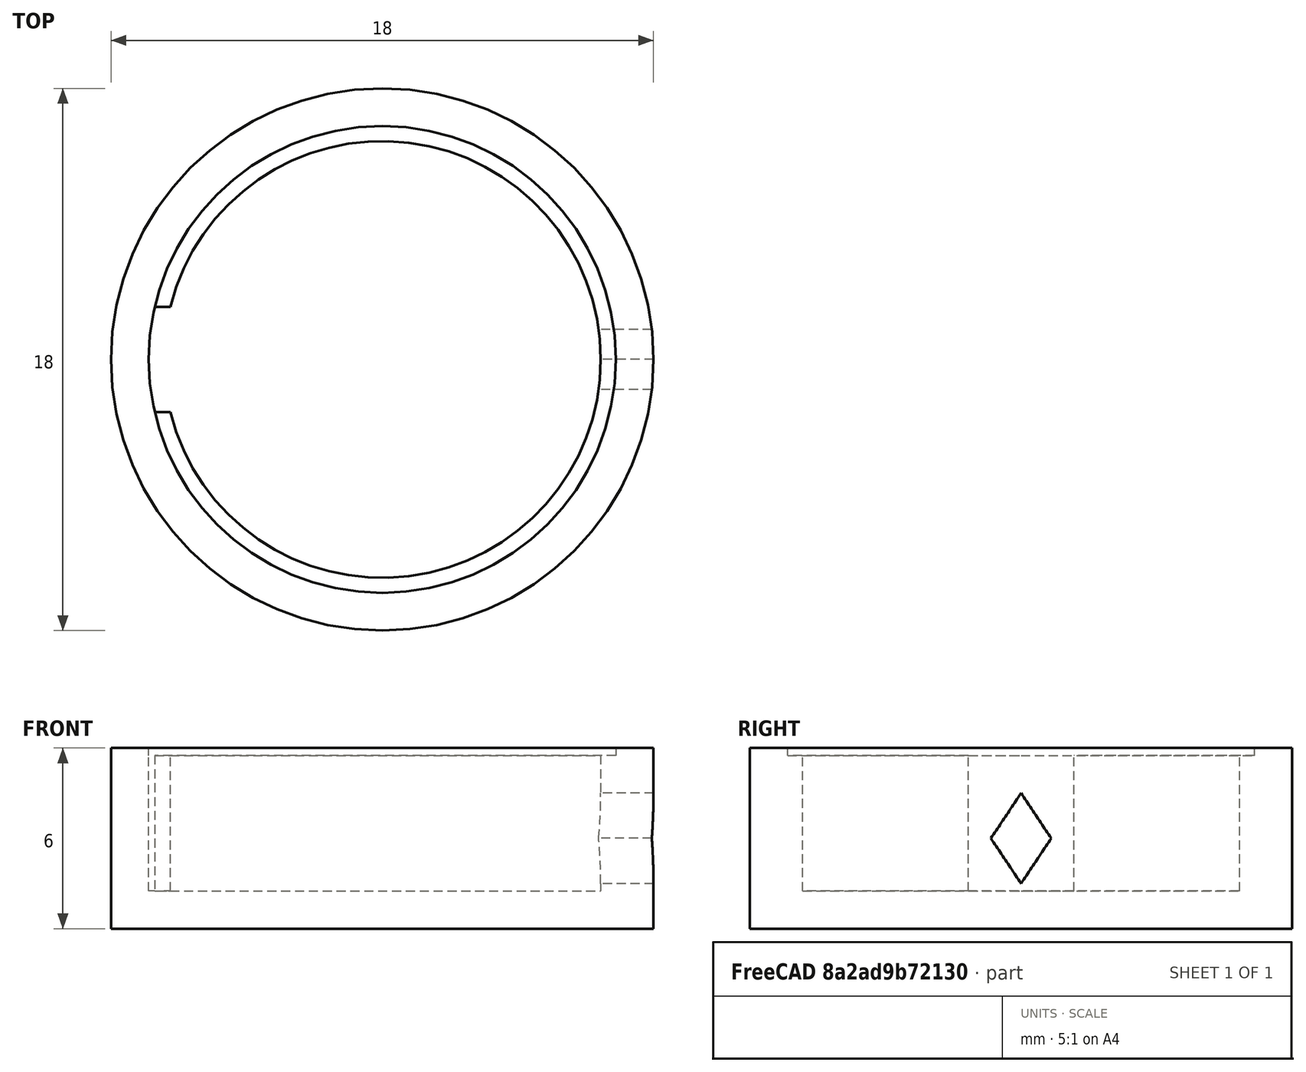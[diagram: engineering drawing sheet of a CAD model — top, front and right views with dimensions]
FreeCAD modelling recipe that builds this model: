
FCSTD DOCUMENT  (FreeCAD 0.17R13541 (Git))
Label: PiezoBlob
License: All rights reserved
LicenseURL: http://en.wikipedia.org/wiki/All_rights_reserved
objects: Sketcher::SketchObject×5, PartDesign::Pocket×4, PartDesign::Pad×1, PartDesign::Plane×1, PartDesign::Body×1, Mesh::Feature×1
note: 17 computed .brp shape members not serialized (recipe doc carries the construction recipe); baked Part::Feature solids carry a one-line shape summary decoded from their .brp

FEATURE [Sketcher::SketchObject] Sketch
  MapMode = 5
  Support = -> [XY_Plane]
  sketch-geometry (2):
    g0: Circle [constr] CenterX=0 CenterY=0 CenterZ=0 NormalX=0 NormalY=0 NormalZ=1 AngleXU=0 Radius=7.5
    g1: Circle CenterX=0 CenterY=0 CenterZ=0 NormalX=0 NormalY=0 NormalZ=1 AngleXU=0 Radius=9
  constraints (4):
    c: Coincident(g0,g-1)
    c: Coincident(g1,g-1)
    c: Radius(g0) = 7.5
    c: Radius(g1) = 9
FEATURE [PartDesign::Pad] Pad
  Length = 6
  Length2 = 100
  Profile = -> Sketch
  Type = 0
FEATURE [Sketcher::SketchObject] Sketch001
  MapMode = 5
  Placement = pos=(0,0,6) rot=(0,0,1;0rad)
  Support = -> [Pad]
  sketch-geometry (1):
    g0: Circle CenterX=0 CenterY=0 CenterZ=0 NormalX=0 NormalY=0 NormalZ=1 AngleXU=0 Radius=7.75
  constraints (2):
    c: Coincident(g0,g-1)
    c: Radius(g0) = 7.75
FEATURE [PartDesign::Pocket] Pocket
  BaseFeature = -> Pad
  Length = 0.25
  Length2 = 100
  Profile = -> Sketch001
  Type = 0
FEATURE [Sketcher::SketchObject] Sketch002
  MapMode = 5
  Placement = pos=(0,0,5.75) rot=(0,0,1;0rad)
  Support = -> [Pocket]
  sketch-geometry (1):
    g0: Circle CenterX=0 CenterY=0 CenterZ=0 NormalX=0 NormalY=0 NormalZ=1 AngleXU=0 Radius=7.25
  constraints (2):
    c: Coincident(g0,g-1)
    c: Radius(g0) = 7.25
FEATURE [PartDesign::Pocket] Pocket001
  BaseFeature = -> Pocket
  Length = 4.5
  Length2 = 100
  Profile = -> Sketch002
  Type = 0
FEATURE [PartDesign::Plane] DatumPlane
  MapMode = 10
  Placement = pos=(9,0,6) rot=(0.57735,0.57735,0.57735;2.0944rad)
  Support = -> [Pocket001]
FEATURE [Sketcher::SketchObject] Sketch003
  MapMode = 5
  Placement = pos=(9,0,6) rot=(0.57735,0.57735,0.57735;2.0944rad)
  Support = -> [DatumPlane]
  sketch-geometry (4):
    g0: LineSegment StartX=0 StartY=-1.5 StartZ=0 EndX=-1 EndY=-3 EndZ=0
    g1: LineSegment StartX=-1 StartY=-3 StartZ=0 EndX=0 EndY=-4.5 EndZ=0
    g2: LineSegment StartX=0 StartY=-1.5 StartZ=0 EndX=1 EndY=-3 EndZ=0
    g3: LineSegment StartX=1 StartY=-3 StartZ=0 EndX=0 EndY=-4.5 EndZ=0
  constraints (12):
    c: PointOnObject(g0,g-2)
    c: Coincident(g1,g0)
    c: PointOnObject(g1,g-2)
    c: PointOnObject(g2,g-2)
    c: Coincident(g3,g2)
    c: Coincident(g3,g1)
    c: Coincident(g2,g0)
    c: Symmetric(g2,g0,g-2)
    c: Distance(g-1,g0) = 1.5
    c: Distance(g0,g1) = 3
    c: DistanceY(g0,g0) = 1.5
    c: DistanceX(g0,g0) = 1
FEATURE [PartDesign::Pocket] Pocket002
  BaseFeature = -> Pocket001
  Length = 5
  Length2 = 100
  Profile = -> Sketch003
  Type = 0
FEATURE [Sketcher::SketchObject] Sketch004
  ExternalGeometry = -> [Pocket002]
  MapMode = 5
  Placement = pos=(0,0,5.75) rot=(0,0,1;0rad)
  Support = -> [Pocket002]
  sketch-geometry (4):
    g0: ArcOfCircle CenterX=0 CenterY=0 CenterZ=0 NormalX=0 NormalY=0 NormalZ=1 AngleXU=0 Radius=7.75 StartAngle=2.91382 EndAngle=3.36936
    g1: LineSegment StartX=-7.54983 StartY=1.75 StartZ=0 EndX=0 EndY=1.75 EndZ=0
    g2: LineSegment StartX=-7.54983 StartY=-1.75 StartZ=0 EndX=0 EndY=-1.75 EndZ=0
    g3: LineSegment StartX=0 StartY=-1.75 StartZ=0 EndX=0 EndY=1.75 EndZ=0
  constraints (12):
    c: Coincident(g0,g-1)
    c: Symmetric(g0,g0,g-1)
    c: Coincident(g1,g0)
    c: PointOnObject(g1,g-2)
    c: Coincident(g2,g0)
    c: PointOnObject(g2,g-2)
    c: Horizontal(g2)
    c: Coincident(g3,g2)
    c: Coincident(g3,g1)
    c: Horizontal(g1)
    c: PointOnObject(g0,g-3)
    c: Distance(g1,g2) = 3.5
FEATURE [PartDesign::Pocket] Pocket003
  BaseFeature = -> Pocket002
  Length = 4.5
  Length2 = 100
  Profile = -> Sketch004
  Type = 0
FEATURE [PartDesign::Body] Body
  Group = -> [Sketch,Pad,Sketch001,Pocket,Sketch002,Pocket001,DatumPlane,Sketch003,Pocket002,Sketch004,Pocket003]
  Origin = -> Origin
  Tip = -> Pocket003
FEATURE [Mesh::Feature] Mesh  label="Body (Meshed)"
